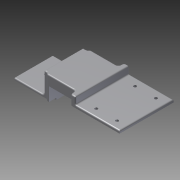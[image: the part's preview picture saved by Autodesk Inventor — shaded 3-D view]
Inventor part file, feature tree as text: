
AUTODESK INVENTOR PART (.ipt)
format: ipt  version: 2012 (Build 160160000, 160)  size: 490,496 bytes
history: native  units: mm
features: extrude x23, sketch x23, projected_geometry x18, reference x11, plane x10, fillet x7, other x1
ambient origin geometry x8: Origin, YZ Plane, XZ Plane, XY Plane, X Axis, Y Axis, Z Axis, Center Point
feature tree (93):
  plane  "Work Plane4"
  extrude  "Extrusion7"  Depth=2.0mm
  plane  "Work Plane5"
  sketch  "Sketch9"  dims[d40=20.0mm d41=0.0mm d42=20.0mm d43=0.0mm]
  plane  "Work Plane6"
  extrude  "Extrusion8"  Depth=20.0mm TaperAngle=0.0deg
  sketch  "Sketch10"  dims[d44=20.0mm d45=0.0mm d46=20.0mm d47=0.0mm]
  plane  "Work Plane7"
  extrude  "Extrusion9"  Depth=20.0mm TaperAngle=0.0deg
  extrude  "Extrusion10"  Depth=20.0mm TaperAngle=0.0deg
  sketch  "Sketch12"  dims[d52=2.0mm d53=0.0mm d54=2.0mm d55=0.0mm]
  plane  "Work Plane8"
  extrude  "Extrusion11"  Depth=2.0mm TaperAngle=0.0deg
  sketch  "Sketch13"  dims[d56=0.3mm d57=0.3mm d58=0.3mm]
  plane  "Work Plane9"
  extrude  "Extrusion12"  Depth=0.3mm
  extrude  "Extrusion13"  Depth=0.3mm
  sketch  "Sketch15"  dims[d62=0.3mm d70=10.0mm d71=0.0mm]
  plane  "Work Plane10"
  extrude  "Extrusion14"  Depth=10.0mm TaperAngle=0.0deg
  plane  "Work Plane11"
  plane  "Work Plane12"
  extrude  "Extrusion17"  Depth=10.0mm TaperAngle=0.0deg
  extrude  "Extrusion18"  Depth=3.75mm
  extrude  "Extrusion19"  Depth=2.5mm
  extrude  "Extrusion20"  Depth=9.0mm
  sketch  "Sketch24"  dims[d87=2.0mm d88=0.0mm]
  plane  "Work Plane13"
  extrude  "Extrusion21"  TaperAngle=0.0deg  [1 undecoded]
  extrude  "Extrusion22"  Depth=9.0mm
  other  "Work Axis1"
  extrude  "Extrusion23"  Depth=4.5mm
  extrude  "Extrusion24"  Depth=0.3mm
  extrude  "Extrusion25"  Depth=0.3mm
  extrude  "Extrusion26"  Depth=25.0mm TaperAngle=0.0deg
  extrude  "Extrusion27"  Depth=2.0mm
  fillet  "Fillet17"  Radius=9.4mm
  fillet  "Fillet18"  Radius=16.76mm
  fillet  "Fillet19"  Radius=33.6mm
  extrude  "Extrusion28"  Depth=9.0mm
  extrude  "Extrusion29"  Depth=4.7mm
  extrude  "Extrusion30"  Depth=10.0mm TaperAngle=0.0deg
  extrude  "Extrusion31"  Depth=0.6mm TaperAngle=0.0deg
  fillet  "Fillet20"  Radius=0.3mm
  fillet  "Fillet21"  Radius=0.3mm
  fillet  "Fillet22"  Radius=0.3mm
  fillet  "Fillet23"  Radius=2.0mm
  sketch  "Sketch8"  dims[d38=2.0mm d39=2.0mm]
  reference  "Reference5"
  reference  "Reference6"
  reference  "Reference7"
  reference  "Reference8"
  projected_geometry  "Projected Loop11"
  reference  "Reference9"
  reference  "Reference10"
  projected_geometry  "Projected Loop12"
  sketch  "Sketch11"  dims[d48=20.0mm d49=0.0mm d50=20.0mm d51=0.0mm]
  projected_geometry  "Projected Loop13"
  reference  "Reference11"
  projected_geometry  "Projected Loop14"
  projected_geometry  "Projected Loop15"
  sketch  "Sketch14"  dims[d60=0.3mm d61=0.3mm]
  projected_geometry  "Projected Loop16"
  projected_geometry  "Projected Loop17"
  sketch  "Sketch19"  dims[d73=2.5mm d74=10.0mm d75=0.0mm]
  sketch  "Sketch20"  dims[d77=7.5mm d79=3.75mm]
  projected_geometry  "Projected Loop23"
  sketch  "Sketch21"  dims[d81=3.75mm d82=2.5mm]
  projected_geometry  "Projected Loop24"
  reference  "Reference19"
  sketch  "Sketch23"  dims[d83=10.0mm d84=0.0mm d86=9.0mm]
  projected_geometry  "Projected Loop25"
  sketch  "Sketch26"  dims[d89=4.5mm d90=9.0mm]
  projected_geometry  "Projected Loop26"
  sketch  "Sketch27"  dims[d91=2.0mm d92=4.5mm]
  projected_geometry  "Projected Loop27"
  sketch  "Sketch28"  dims[d103=0.3mm d104=0.3mm]
  projected_geometry  "Projected Loop28"
  sketch  "Sketch29"  dims[d105=0.3mm d106=0.3mm]
  projected_geometry  "Projected Loop29"
  sketch  "Sketch30"  dims[d107=10.0mm d108=0.0mm d110=25.0mm d111=0.0mm]
  projected_geometry  "Projected Loop30"
  sketch  "Sketch32"  dims[d112=0.3mm d113=2.0mm d114=9.4mm d115=16.76mm d116=33.6mm]
  projected_geometry  "Projected Loop31"
  sketch  "Sketch33"  dims[d117=8.42mm d118=9.0mm]
  projected_geometry  "Projected Loop32"
  sketch  "Sketch34"  dims[d119=8.38mm d120=4.7mm]
  projected_geometry  "Projected Loop33"
  sketch  "Sketch35"  dims[d121=4.0mm d122=10.0mm d123=0.0mm]
  sketch  "Sketch36"  dims[d124=0.3mm d125=0.0mm d126=0.6mm d127=0.0mm d128=0.3mm d129=0.0mm d130=0.3mm d131=0.0mm d132=0.3mm d133=0.0mm d138=2.0mm d139=1.0mm d140=1.0mm d141=10.0mm d142=0.0mm d143=2.0mm d144=0.0mm d145=30.5mm d146=8.5mm d147=0.0mm d148=0.0mm d149=30.5mm d150=0.0mm d151=2.0mm d152=2.0mm d153=1.0mm d154=1.0mm d155=2.5mm d156=23.25mm d157=11.625mm d158=11.625mm d159=4.5mm d160=4.5mm d161=2.5mm d162=4.5mm d163=2.5mm]
  reference  "Reference21"
  reference  "Reference22"
  reference  "Reference23"
note: 1 required parameter value undecoded (feature->parameter linkage not recoverable at this tier; creation-order binding heuristic only, values carry confidence <= 0.55)
